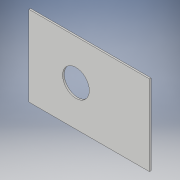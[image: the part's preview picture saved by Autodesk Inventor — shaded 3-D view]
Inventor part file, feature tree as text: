
AUTODESK INVENTOR PART (.ipt)
format: ipt  version: 2017 (Build 210142000, 142)  size: 96,256 bytes
history: native  units: in
note: dims shown in document units (in); Inventor stores cm internally (conversion verified against a paired STEP export)
features: sketch x2, extrude x1
ambient origin geometry x8: Origin, YZ Plane, XZ Plane, XY Plane, X Axis, Y Axis, Z Axis, Center Point
bodies: Solid1 (feature_tree)
feature tree (3):
  sketch  "Sketch1"  dims[d0=18.0in d1=12.0in]
  sketch  "Sketch2"  dims[d4=4.0in d5=0.25in d6=0.0in]
  extrude  "Extrusion1"  Depth=12.0in
